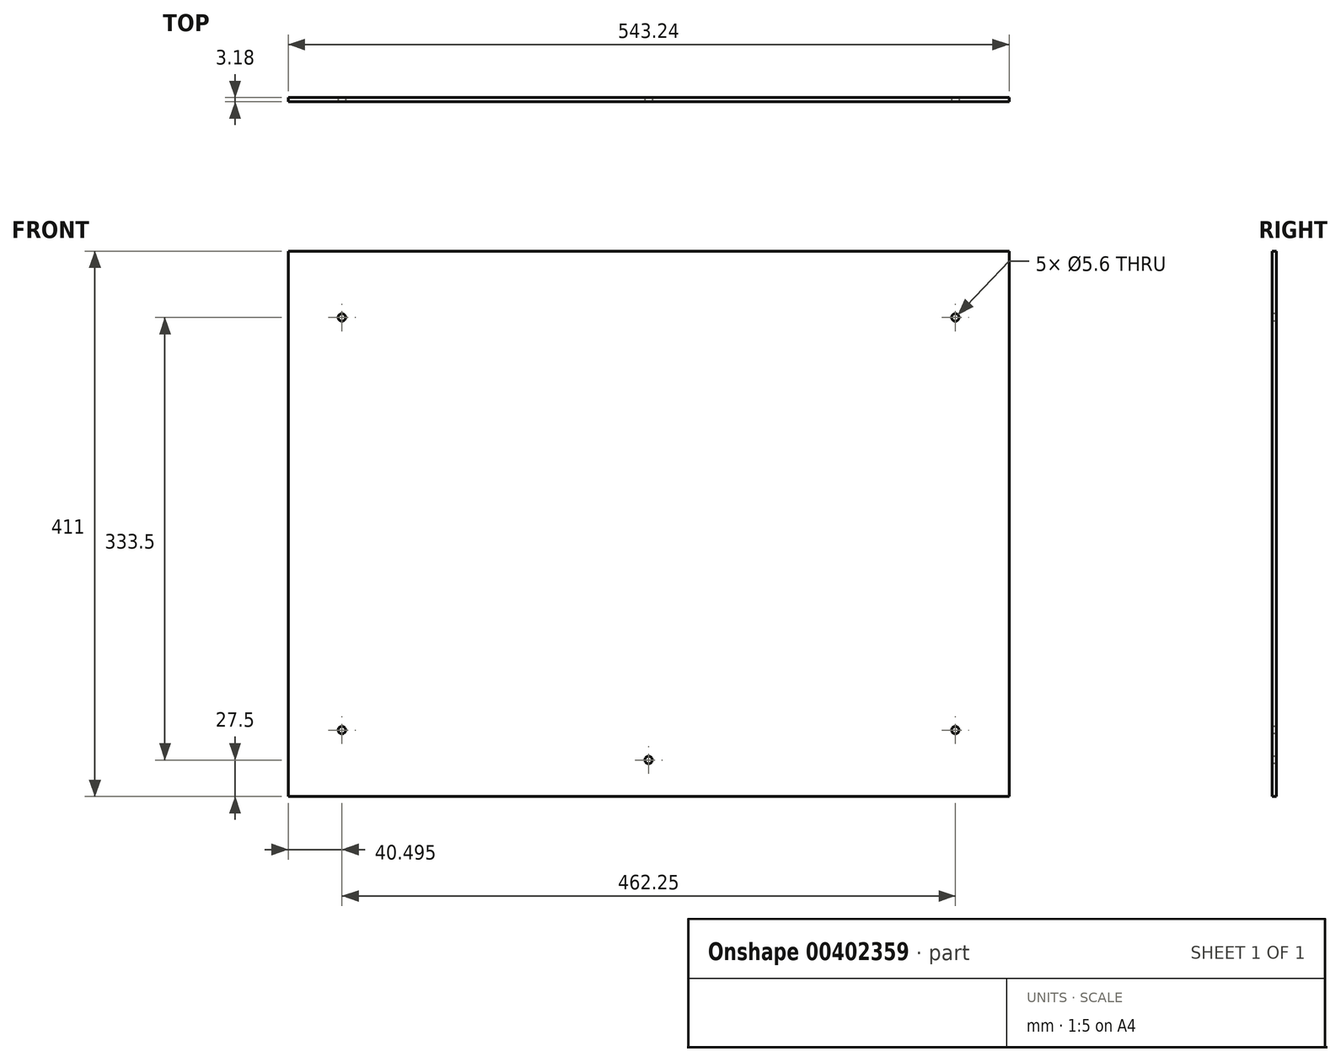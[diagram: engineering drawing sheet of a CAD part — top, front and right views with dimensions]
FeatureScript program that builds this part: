
annotation { "Feature Type Name" : "Feature", "Feature Type Description" : "" }
export const myFeature = defineFeature(function(context is Context, id is Id, definition is map)
    precondition{}
    {
        {
            var Q0;
            Q0=qCreatedBy(makeId("Front.planeOp"),FACE);
            var sketch = newSketch(context, id + "F0", { "sketchPlane" : qUnion([Q0])});
            skLineSegment(sketch, "E0.bottom", {"start": v(-271.62, 205.5) * mm, "end": v(271.62, 205.5) * mm});
            skLineSegment(sketch, "E0.top", {"start": v(-271.63, -205.5) * mm, "end": v(271.62, -205.5) * mm});
            skLineSegment(sketch, "E0.left", {"start": v(-271.62, 205.5) * mm, "end": v(-271.63, -205.5) * mm});
            skLineSegment(sketch, "E0.right", {"start": v(271.62, 205.5) * mm, "end": v(271.62, -205.5) * mm});
            skPoint(sketch, "E0.middle", {"position": v(0, 0) * mm});
            skSolve(sketch);
        }
        {
            var Q0;
            Q0=makeQuery(id+"F0.imprint","IMPRINT",FACE,{"disambiguationData":[TD([[makeQuery(id+"F0.imprint","IMPRINT",EDGE,{"derivedFrom":sQuery(id+"F0.wireOp",EDGE,"E0.bottom")}),-1.0]])]});
            extrude(context, id + "F1", {"entities" : qUnion([Q0]), "depth" : (.125 * 25.4) * mm});
        }
        {
            var Q0;
            Q0=makeQuery(id+"F1.opExtrude","CAP_FACE",FACE,{"disambiguationData":[OSD([sQuery(id+"F0.wireOp",EDGE,"E0.bottom"),sQuery(id+"F0.wireOp",EDGE,"E0.top"),sQuery(id+"F0.wireOp",EDGE,"E0.left"),sQuery(id+"F0.wireOp",EDGE,"E0.right")])],"isStart":false});
            var sketch = newSketch(context, id + "F2", { "sketchPlane" : qUnion([Q0])});
            skCircle(sketch, "E1", {"center": v(-231.12, 155.5) * mm, "radius": 2.8 * mm});
            skCircle(sketch, "E2", {"center": v(-231.13, -155.5) * mm, "radius": 2.8 * mm});
            skCircle(sketch, "E3", {"center": v(0, -178) * mm, "radius": 2.8 * mm});
            skCircle(sketch, "E4", {"center": v(231.12, -155.5) * mm, "radius": 2.8 * mm});
            skCircle(sketch, "E5", {"center": v(231.12, 155.5) * mm, "radius": 2.8 * mm});
            skSolve(sketch);
        }
        {
            var Q0;
            Q0 = qSketchRegion(id + "F2", true);
            extrude(context, id + "F3", {"entities" : qUnion([Q0]), "operationType" : NewBodyOperationType.REMOVE, "oppositeDirection" : true, "depth" : 25 * mm});
        }
    });
